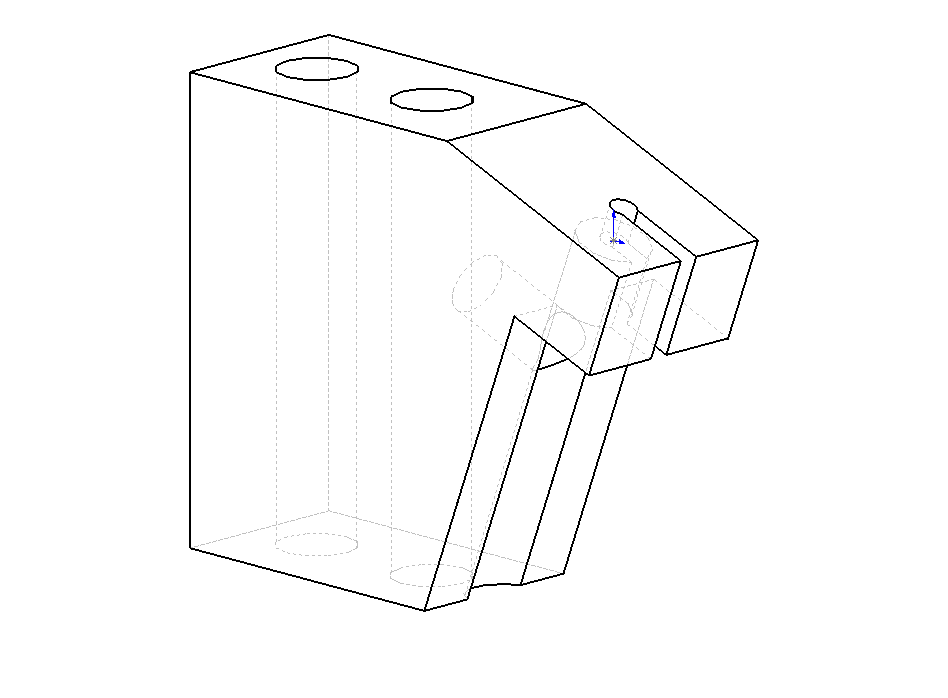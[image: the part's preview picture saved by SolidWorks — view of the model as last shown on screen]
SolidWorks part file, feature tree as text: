
SOLIDWORKS PART (.sldprt)
format: sldprt  version: not decoded by parser v0  size: 621,056 bytes
history: native  units: mm
features: sketch x12, cut_extrude x6, extrude x4, material x1, plane x1, hole x1 (+12 scaffold rows collapsed)
feature tree (37):
  scaffold x12  (default folders/planes/origin — collapsed)
  material  "Material <not specified>"
  sketch  "Sketch1"  dims[c1.D1=~23.614254mm c2.D1=21.07deg c2.D2=16.51mm c2.D3=17.78mm c2.D4=16.0mm c2.D5=20.0mm c3.D2=17.78mm c3.D3=16.51mm c4.D2=16.51mm c4.D6=8.0mm c4.D7=4.0mm c5.D6=12.0mm c5.D7=10.0mm c6.D6=3.35mm c6.D7=~30.015838mm c6.D4=25.0mm c7.D6=5.07mm]
  extrude  "Base-Extrude"  Depth=10mm
  sketch  "Sketch2"  dims[D1=4.0mm D2=9.0mm]
  cut_extrude  "Cutaway for Clamp Plate & Wire"  [1 undecoded]
  sketch  "Sketch3"  dims[c1.D1=4.826mm c1.D4=4.572mm c1.D2=8.0mm c2.D2=90.0deg c2.D3=~4.003032mm c2.D4=4.1275mm c2.D5=8.255mm c3.D3=4.0mm]
  cut_extrude  "Clamp Plate Holes (altered to #10-24 OCT04)"  [1 undecoded]
  sketch  "Sketch4"  dims[D1=4.3053mm D2=8.255mm]
  cut_extrude  "Holes to Pitch Plate"  [1 undecoded]
  sketch  "Sketch5"  dims[D1=4.1mm D2=10.0mm]
  extrude  "Extrude1"  Depth=4mm
  plane  "Plane1"  Offset=0mm
  sketch  "Sketch6"  dims[D1=1.5mm]
  extrude  "Extrude2"  Depth=2mm
  sketch  "Sketch8"
  extrude  "Extrude3"  [1 undecoded]
  sketch  "Sketch7"
  cut_extrude  "Cut-Extrude1"  [1 undecoded]
  sketch  "Sketch11"
  cut_extrude  "Cut-Extrude2"  [1 undecoded]
  sketch  "Sketch12"  dims[D1=1.1mm]
  cut_extrude  "Cut-Extrude3"  [1 undecoded]
  hole  "#8-32 Tapped Hole1"  Diameter=3.4544mm Depth=6.858mm
  sketch  "Sketch14"  dims[D1=3.429mm]
  sketch  "Sketch13"  dims[hole-wizard template sketch: 47 standard entries collapsed; hole parameters kept: c15.Tap Drill Depth=6.858mm c15.D3=~14.816244mm c15.Drill Angle=118.0deg]
decode coverage: 13 of 23 modeling features carry decoded parameters
note: ~ marks probable driven/reference dimensions
note: 7 parameter values undecoded
summary: no parameter record found for 7 features
note: suppression state not decoded; provenance and decode notes live in map.json
